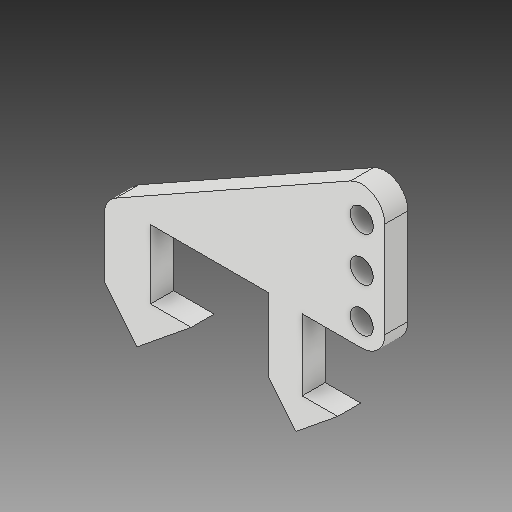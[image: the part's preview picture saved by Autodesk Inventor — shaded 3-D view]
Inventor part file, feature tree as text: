
AUTODESK INVENTOR PART (.ipt)
format: ipt  version: 2017 (Build 210142000, 142)  size: 120,832 bytes
history: native  units: mm
features: extrude x1, sketch x1
ambient origin geometry x8: Origin, YZ Plane, XZ Plane, XY Plane, X Axis, Y Axis, Z Axis, Center Point
bodies: Solid1 (feature_tree)
feature tree (2):
  extrude  "Extrusion1"  Depth=2.0mm
  sketch  "Sketch1"  dims[d0=2.0mm d1=2.0mm d2=2.0mm d3=2.0mm d4=2.0mm d5=0.0mm]
